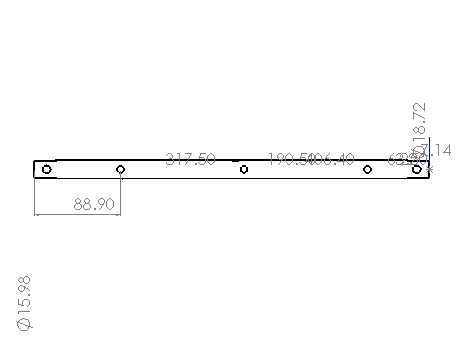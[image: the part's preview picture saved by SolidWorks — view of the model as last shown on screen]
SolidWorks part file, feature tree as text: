
SOLIDWORKS PART (.sldprt)
format: sldprt  version: not decoded by parser v0  size: 342,528 bytes
history: native  units: mm
features: sketch x11, cut_extrude x10, material x1, extrude x1 + 1 further entry (+14 scaffold rows collapsed)
feature tree (38):
  scaffold x14  (default folders/planes/origin — collapsed)
  material  "Material <not specified>"
  "Annotations"  RD3=15.98mm RD2=406.4mm RD1=18.72mm RD4=63.5mm RD5=190.5mm RD6=317.5mm RD7=88.9mm RD8=22mm RD9=7.14mm
  sketch  "Sketch1"  dims[D1=7.875mm]
  extrude  "Extrude1"  Depth=406.4mm
  sketch  "Sketch2"  dims[D1=12.7mm D2=12.7mm]
  cut_extrude  "Cut-Extrude1"  [1 undecoded]
  sketch  "Sketch4"  dims[D1=~4.09807mm]
  cut_extrude  "Cut-Extrude4"  [1 undecoded]
  sketch  "Sketch5"
  cut_extrude  "Cut-Extrude5"  [1 undecoded]
  sketch  "Sketch6"
  cut_extrude  "Cut-Extrude6"  [1 undecoded]
  sketch  "Sketch7"  dims[D1=~3.63587mm]
  cut_extrude  "Cut-Extrude7"  [1 undecoded]
  sketch  "Sketch8"  dims[D1=~3.731074mm]
  cut_extrude  "Cut-Extrude9"  [1 undecoded]
  sketch  "Sketch9"  dims[D1=~3.373033mm]
  cut_extrude  "Cut-Extrude10"  [1 undecoded]
  sketch  "Sketch10"  dims[D1=~1.428521mm]
  cut_extrude  "Cut-Extrude11"  [1 undecoded]
  sketch  "Sketch11"  dims[D1=~4.07695mm]
  cut_extrude  "Cut-Extrude12"  [1 undecoded]
  sketch  "Sketch12"  dims[D1=~2.771953mm]
  cut_extrude  "Cut-Extrude13"  [1 undecoded]
decode coverage: 10 of 22 modeling features carry decoded parameters; 1 rows unclassified (native names shown)
note: ~ marks probable driven/reference dimensions
note: 10 parameter values undecoded
summary: no parameter record found for 10 features
note: suppression state not decoded; provenance and decode notes live in map.json
